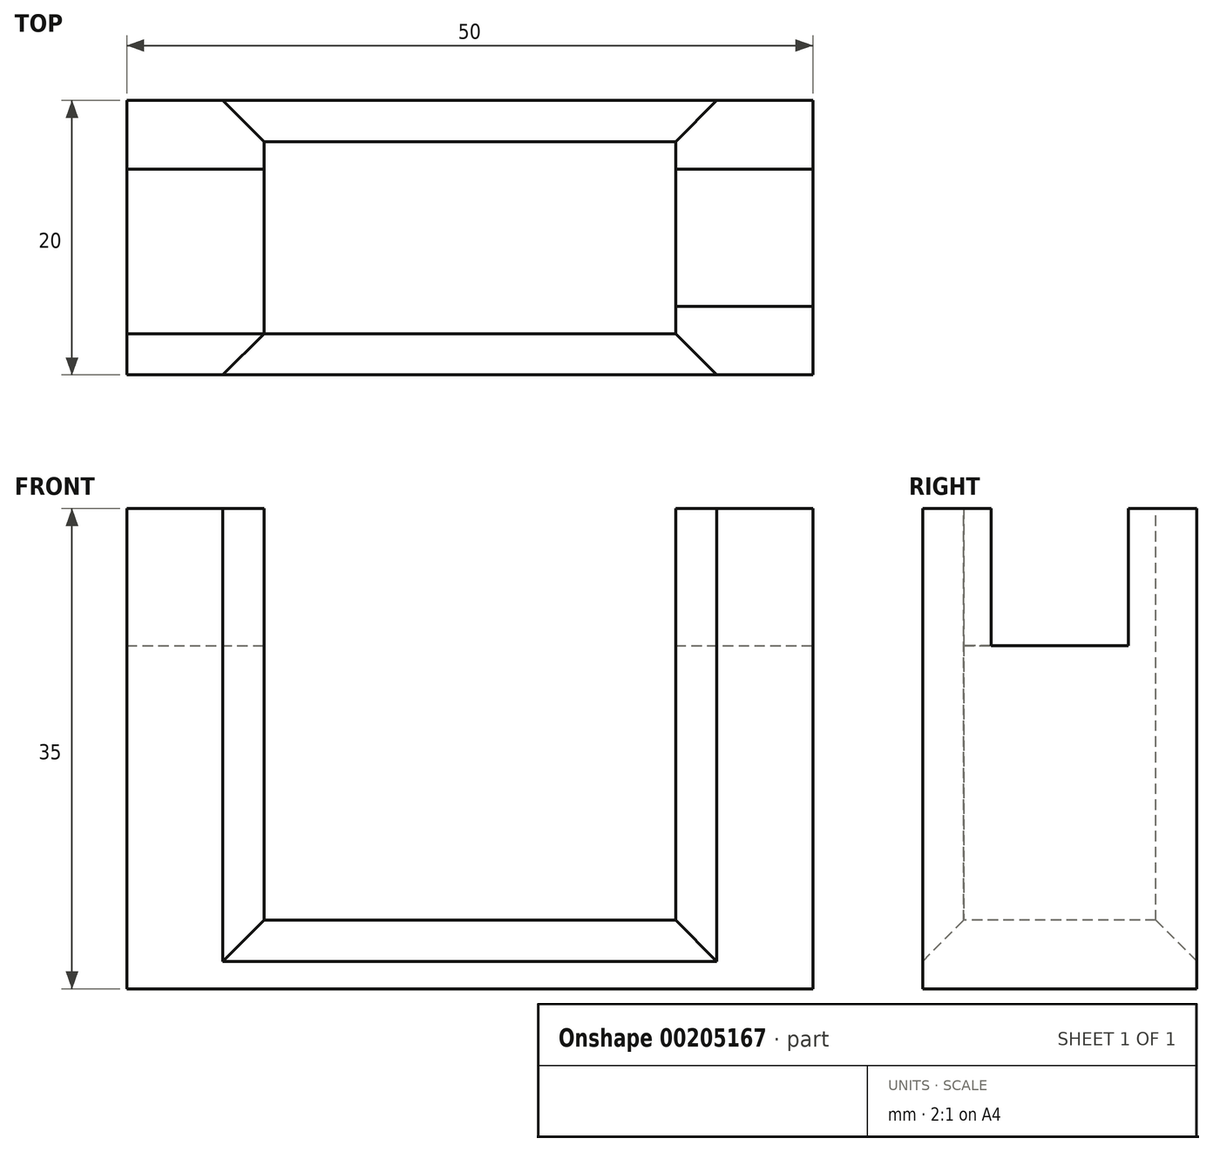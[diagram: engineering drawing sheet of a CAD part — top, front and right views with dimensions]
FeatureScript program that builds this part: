
annotation { "Feature Type Name" : "Feature", "Feature Type Description" : "" }
export const myFeature = defineFeature(function(context is Context, id is Id, definition is map)
    precondition{}
    {
        {
            var Q0;
            Q0=qCreatedBy(makeId("Top.planeOp"),FACE);
            var sketch = newSketch(context, id + "F0", { "sketchPlane" : qUnion([Q0])});
            skLineSegment(sketch, "E0.bottom", {"start": v(25, -10) * mm, "end": v(-25, -10) * mm});
            skLineSegment(sketch, "E0.top", {"start": v(25, 10) * mm, "end": v(-25, 10) * mm});
            skLineSegment(sketch, "E0.left", {"start": v(25, -10) * mm, "end": v(25, 10) * mm});
            skLineSegment(sketch, "E0.right", {"start": v(-25, -10) * mm, "end": v(-25, 10) * mm});
            skPoint(sketch, "E0.middle", {"position": v(0, 0) * mm});
            skSolve(sketch);
        }
        {
            var Q0;
            Q0=makeQuery(id+"F0.imprint","IMPRINT",FACE,{"disambiguationData":[TD([[makeQuery(id+"F0.imprint","IMPRINT",EDGE,{"derivedFrom":sQuery(id+"F0.wireOp",EDGE,"E0.bottom")}),-1.0]])]});
            extrude(context, id + "F1", {"entities" : qUnion([Q0]), "depth" : 5 * mm});
        }
        {
            var Q0;
            Q0=makeQuery(id+"F1.opExtrude","CAP_FACE",FACE,{"disambiguationData":[OSD([sQuery(id+"F0.wireOp",EDGE,"E0.bottom"),sQuery(id+"F0.wireOp",EDGE,"E0.top"),sQuery(id+"F0.wireOp",EDGE,"E0.left"),sQuery(id+"F0.wireOp",EDGE,"E0.right")])],"isStart":false});
            var sketch = newSketch(context, id + "F2", { "sketchPlane" : qUnion([Q0])});
            skLineSegment(sketch, "E1.bottom", {"start": v(-25, 10) * mm, "end": v(-15, 10) * mm});
            skLineSegment(sketch, "E1.top", {"start": v(-25, -10) * mm, "end": v(-15, -10) * mm});
            skLineSegment(sketch, "E1.left", {"start": v(-25, 10) * mm, "end": v(-25, -10) * mm});
            skLineSegment(sketch, "E1.right", {"start": v(-15, 10) * mm, "end": v(-15, -10) * mm});
            skLineSegment(sketch, "E2.bottom", {"start": v(25, 10) * mm, "end": v(15, 10) * mm});
            skLineSegment(sketch, "E2.top", {"start": v(25, -10) * mm, "end": v(15, -10) * mm});
            skLineSegment(sketch, "E2.left", {"start": v(25, 10) * mm, "end": v(25, -10) * mm});
            skLineSegment(sketch, "E2.right", {"start": v(15, 10) * mm, "end": v(15, -10) * mm});
            skSolve(sketch);
        }
        {
            var Q0;
            Q0=makeQuery(id+"F2.imprint","IMPRINT",FACE,{"disambiguationData":[TD([[makeQuery(id+"F2.imprint","IMPRINT",EDGE,{"derivedFrom":sQuery(id+"F2.wireOp",EDGE,"E1.bottom")}),1.0]])]});
            var Q1;
            Q1=makeQuery(id+"F2.imprint","IMPRINT",FACE,{"disambiguationData":[TD([[makeQuery(id+"F2.imprint","IMPRINT",EDGE,{"derivedFrom":sQuery(id+"F2.wireOp",EDGE,"E2.bottom")}),1.0]])]});
            extrude(context, id + "F3", {"entities" : qUnion([Q0, Q1]), "operationType" : NewBodyOperationType.ADD, "depth" : 20 * mm});
        }
        {
            var Q0;
            Q0=makeQuery(id+"F3.opExtrude","SWEPT_EDGE",EDGE,{"disambiguationData":[OSD([sQuery(id+"F0.wireOp",EDGE,"E0.bottom"),sQuery(id+"F2.wireOp",EDGE,"E1.top"),sQuery(id+"F2.wireOp",EDGE,"E1.right")])]});
            var Q1;
            Q1=makeQuery(id+"F3.opExtrude","SWEPT_EDGE",EDGE,{"disambiguationData":[OSD([sQuery(id+"F0.wireOp",EDGE,"E0.top"),sQuery(id+"F2.wireOp",EDGE,"E1.bottom"),sQuery(id+"F2.wireOp",EDGE,"E1.right")])]});
            var Q2;
            Q2=makeQuery(id+"F3.opExtrude","SWEPT_EDGE",EDGE,{"disambiguationData":[OSD([sQuery(id+"F0.wireOp",EDGE,"E0.top"),sQuery(id+"F2.wireOp",EDGE,"E2.bottom"),sQuery(id+"F2.wireOp",EDGE,"E2.right")])]});
            var Q3;
            Q3=makeQuery(id+"F3.opExtrude","SWEPT_EDGE",EDGE,{"disambiguationData":[OSD([sQuery(id+"F0.wireOp",EDGE,"E0.bottom"),sQuery(id+"F2.wireOp",EDGE,"E2.top"),sQuery(id+"F2.wireOp",EDGE,"E2.right")])]});
            chamfer(context, id + "F4", {"entities" : qUnion([Q0, Q1, Q2, Q3]), "width" : 3 * mm, "tangentPropagation" : true});
        }
        {
            var Q0;
            Q0=makeQuery(id+"F3.opExtrude","CAP_FACE",FACE,{"disambiguationData":[OSD([sQuery(id+"F2.wireOp",EDGE,"E1.bottom"),sQuery(id+"F2.wireOp",EDGE,"E1.top"),sQuery(id+"F2.wireOp",EDGE,"E1.left"),sQuery(id+"F2.wireOp",EDGE,"E1.right")])],"isStart":false});
            var sketch = newSketch(context, id + "F5", { "sketchPlane" : qUnion([Q0])});
            skLineSegment(sketch, "E3", {"start": v(-18, -10) * mm, "end": v(-15, -7) * mm});
            skLineSegment(sketch, "E4", {"start": v(-15, -7) * mm, "end": v(-25, -7) * mm});
            skLineSegment(sketch, "E5", {"start": v(-25, -7) * mm, "end": v(-25, -10) * mm});
            skLineSegment(sketch, "E6", {"start": v(-25, -10) * mm, "end": v(-18, -10) * mm});
            skLineSegment(sketch, "E7", {"start": v(-15, 7) * mm, "end": v(-18, 10) * mm});
            skLineSegment(sketch, "E8", {"start": v(-18, 10) * mm, "end": v(-25, 10) * mm});
            skLineSegment(sketch, "E9", {"start": v(-25, 10) * mm, "end": v(-25, 7) * mm});
            skLineSegment(sketch, "E10", {"start": v(-25, 7) * mm, "end": v(-15, 7) * mm});
            skLineSegment(sketch, "E11.bottom", {"start": v(-25, -7) * mm, "end": v(-15, -7) * mm});
            skLineSegment(sketch, "E11.top", {"start": v(-25, -5) * mm, "end": v(-15, -5) * mm});
            skLineSegment(sketch, "E11.left", {"start": v(-25, -7) * mm, "end": v(-25, -5) * mm});
            skLineSegment(sketch, "E11.right", {"start": v(-15, -7) * mm, "end": v(-15, -5) * mm});
            skLineSegment(sketch, "E12.top", {"start": v(-25, 5) * mm, "end": v(-15, 5) * mm});
            skLineSegment(sketch, "E12.left", {"start": v(-25, 7) * mm, "end": v(-25, 5) * mm});
            skLineSegment(sketch, "E12.right", {"start": v(-15, 7) * mm, "end": v(-15, 5) * mm});
            skSolve(sketch);
        }
        {
            var Q0;
            Q0=makeQuery(id+"F5.imprint","IMPRINT",FACE,{"disambiguationData":[TD([[makeQuery(id+"F5.imprint","IMPRINT",EDGE,{"derivedFrom":sQuery(id+"F5.wireOp",EDGE,"E3")}),1.0]])]});
            var Q1;
            Q1=makeQuery(id+"F5.imprint","IMPRINT",FACE,{"disambiguationData":[TD([[makeQuery(id+"F5.imprint","IMPRINT",EDGE,{"derivedFrom":sQuery(id+"F5.wireOp",EDGE,"E11.bottom")}),1.0]])]});
            var Q2;
            Q2=makeQuery(id+"F5.imprint","IMPRINT",FACE,{"disambiguationData":[TD([[makeQuery(id+"F5.imprint","IMPRINT",EDGE,{"derivedFrom":sQuery(id+"F5.wireOp",EDGE,"E10")}),-1.0]])]});
            var Q3;
            Q3=makeQuery(id+"F5.imprint","IMPRINT",FACE,{"disambiguationData":[TD([[makeQuery(id+"F5.imprint","IMPRINT",EDGE,{"derivedFrom":sQuery(id+"F5.wireOp",EDGE,"E7")}),1.0]])]});
            extrude(context, id + "F6", {"entities" : qUnion([Q0, Q1, Q2, Q3]), "operationType" : NewBodyOperationType.ADD, "depth" : 10 * mm});
        }
        {
            var Q0;
            Q0=makeQuery(id+"F3.opExtrude","CAP_FACE",FACE,{"disambiguationData":[OSD([sQuery(id+"F2.wireOp",EDGE,"E2.bottom"),sQuery(id+"F2.wireOp",EDGE,"E2.top"),sQuery(id+"F2.wireOp",EDGE,"E2.left"),sQuery(id+"F2.wireOp",EDGE,"E2.right")])],"isStart":false});
            var sketch = newSketch(context, id + "F7", { "sketchPlane" : qUnion([Q0])});
            skLineSegment(sketch, "E13", {"start": v(18, 10) * mm, "end": v(15, 7) * mm});
            skLineSegment(sketch, "E14", {"start": v(15, 7) * mm, "end": v(15, 5) * mm});
            skLineSegment(sketch, "E15", {"start": v(15, 5) * mm, "end": v(25, 5) * mm});
            skLineSegment(sketch, "E16", {"start": v(25, 5) * mm, "end": v(25, 10) * mm});
            skLineSegment(sketch, "E17", {"start": v(25, 10) * mm, "end": v(18, 10) * mm});
            skLineSegment(sketch, "E18", {"start": v(25, -10) * mm, "end": v(18, -10) * mm});
            skLineSegment(sketch, "E19", {"start": v(18, -10) * mm, "end": v(15, -7) * mm});
            skLineSegment(sketch, "E20", {"start": v(15, -7) * mm, "end": v(15, -5) * mm});
            skLineSegment(sketch, "E21", {"start": v(15, -5) * mm, "end": v(25, -5) * mm});
            skLineSegment(sketch, "E22", {"start": v(25, -5) * mm, "end": v(25, -10) * mm});
            skSolve(sketch);
        }
        {
            var Q0;
            Q0=makeQuery(id+"F7.imprint","IMPRINT",FACE,{"disambiguationData":[TD([[makeQuery(id+"F7.imprint","IMPRINT",EDGE,{"derivedFrom":sQuery(id+"F7.wireOp",EDGE,"E13")}),1.0]])]});
            var Q1;
            Q1=makeQuery(id+"F7.imprint","IMPRINT",FACE,{"disambiguationData":[TD([[makeQuery(id+"F7.imprint","IMPRINT",EDGE,{"derivedFrom":sQuery(id+"F7.wireOp",EDGE,"E18")}),-1.0]])]});
            extrude(context, id + "F8", {"entities" : qUnion([Q0, Q1]), "operationType" : NewBodyOperationType.ADD, "depth" : 10 * mm});
        }
        {
            var Q0;
            Q0=makeQuery(id+"F1.opExtrude","CAP_EDGE",EDGE,{"disambiguationData":[OSD([sQuery(id+"F0.wireOp",EDGE,"E0.bottom")])],"isStart":false});
            var Q1;
            Q1=makeQuery(id+"F1.opExtrude","CAP_EDGE",EDGE,{"disambiguationData":[OSD([sQuery(id+"F0.wireOp",EDGE,"E0.top")])],"isStart":false});
            chamfer(context, id + "F9", {"entities" : qUnion([Q0, Q1]), "width" : 3 * mm, "tangentPropagation" : true});
        }
    });
